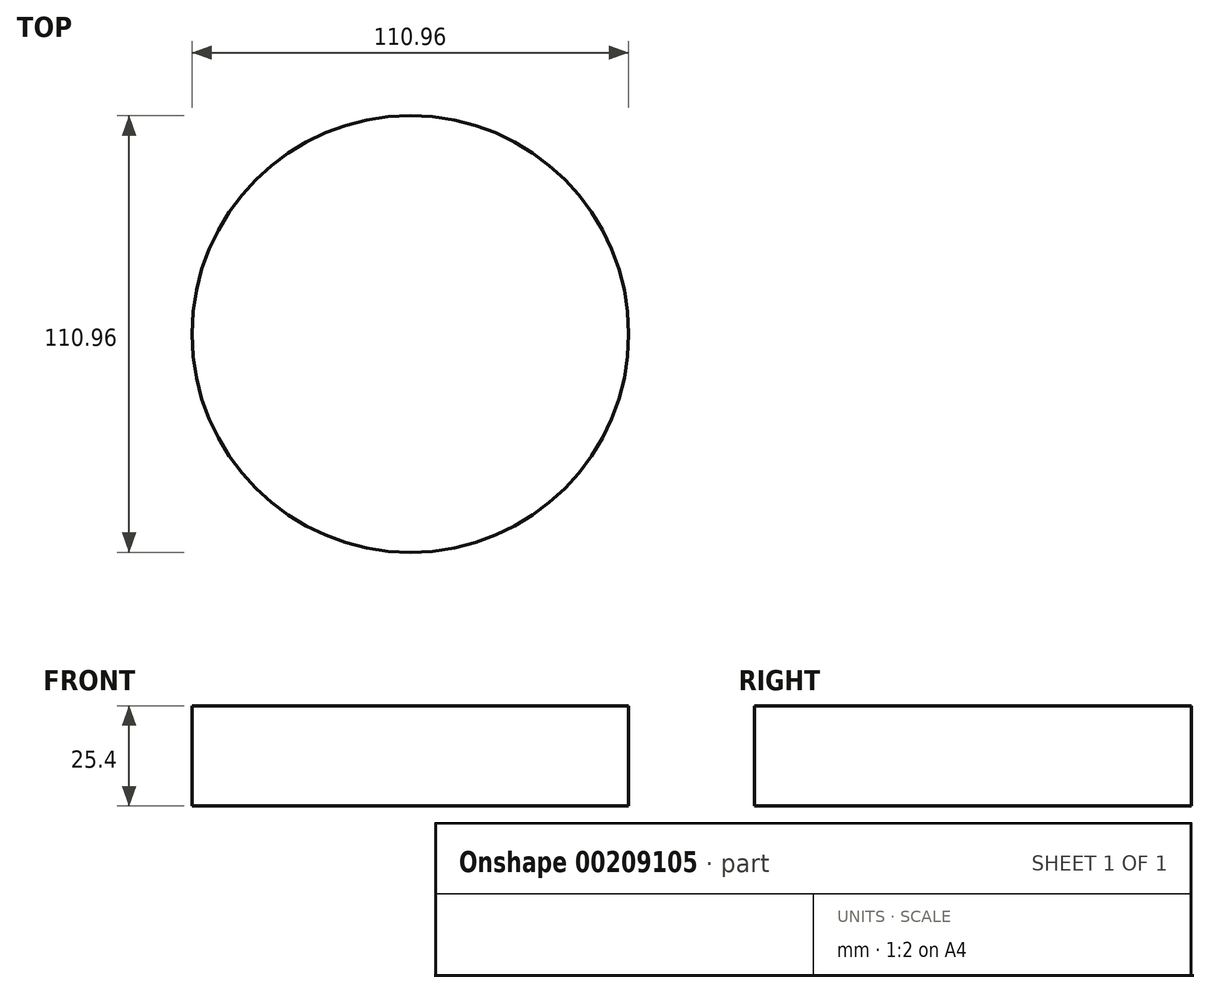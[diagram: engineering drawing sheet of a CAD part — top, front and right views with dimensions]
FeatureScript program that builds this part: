
annotation { "Feature Type Name" : "Feature", "Feature Type Description" : "" }
export const myFeature = defineFeature(function(context is Context, id is Id, definition is map)
    precondition{}
    {
        {
            var Q0;
            Q0=qCreatedBy(makeId("Top.planeOp"),FACE);
            var sketch = newSketch(context, id + "F0", { "sketchPlane" : qUnion([Q0])});
            skCircle(sketch, "E0", {"center": v(0, 0) * mm, "radius": 55.48 * mm});
            skSolve(sketch);
        }
        {
            var Q0;
            Q0 = qSketchRegion(id + "F0", true);
            extrude(context, id + "F1", {"entities" : qUnion([Q0]), "depth" : 25.4 * mm});
        }
    });
